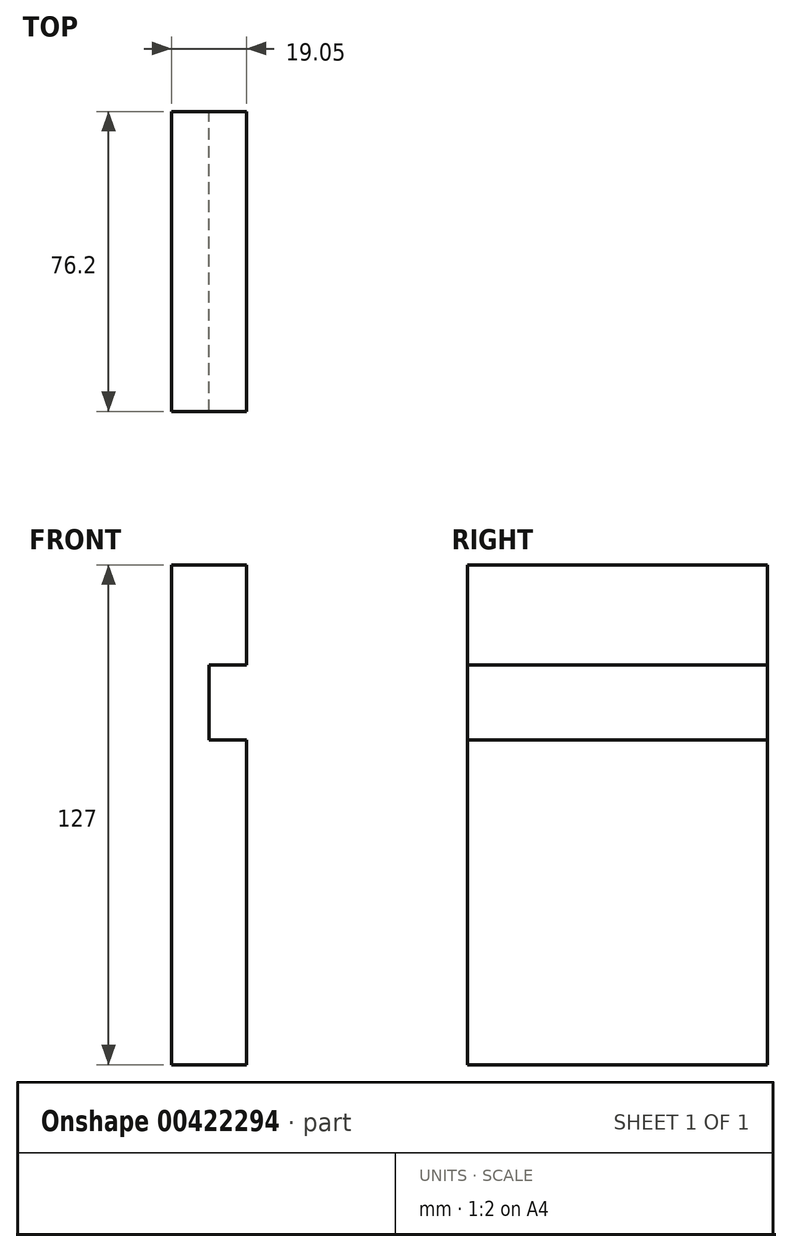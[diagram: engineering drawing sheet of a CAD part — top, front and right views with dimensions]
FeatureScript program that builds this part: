
annotation { "Feature Type Name" : "Feature", "Feature Type Description" : "" }
export const myFeature = defineFeature(function(context is Context, id is Id, definition is map)
    precondition{}
    {
        {
            var Q0;
            Q0=qCreatedBy(makeId("Front.planeOp"),FACE);
            var sketch = newSketch(context, id + "F0", { "sketchPlane" : qUnion([Q0])});
            skLineSegment(sketch, "E0", {"start": v(-40.45, 74.22) * mm, "end": v(-40.45, -52.78) * mm});
            skLineSegment(sketch, "E1", {"start": v(-40.45, -52.78) * mm, "end": v(-21.4, -52.78) * mm});
            skLineSegment(sketch, "E2", {"start": v(-40.45, 74.22) * mm, "end": v(-21.4, 74.22) * mm});
            skLineSegment(sketch, "E3", {"start": v(-21.4, 74.22) * mm, "end": v(-21.4, 48.82) * mm});
            skLineSegment(sketch, "E4", {"start": v(-21.4, 48.82) * mm, "end": v(-30.92, 48.82) * mm});
            skLineSegment(sketch, "E5", {"start": v(-30.92, 48.82) * mm, "end": v(-30.92, 29.77) * mm});
            skLineSegment(sketch, "E6", {"start": v(-30.92, 29.77) * mm, "end": v(-21.4, 29.77) * mm});
            skLineSegment(sketch, "E7", {"start": v(-21.4, 29.77) * mm, "end": v(-21.4, -52.78) * mm});
            skSolve(sketch);
        }
        {
            var Q0;
            Q0 = qSketchRegion(id + "F0", true);
            extrude(context, id + "F1", {"entities" : qUnion([Q0]), "depth" : 76.2 * mm});
        }
    });
